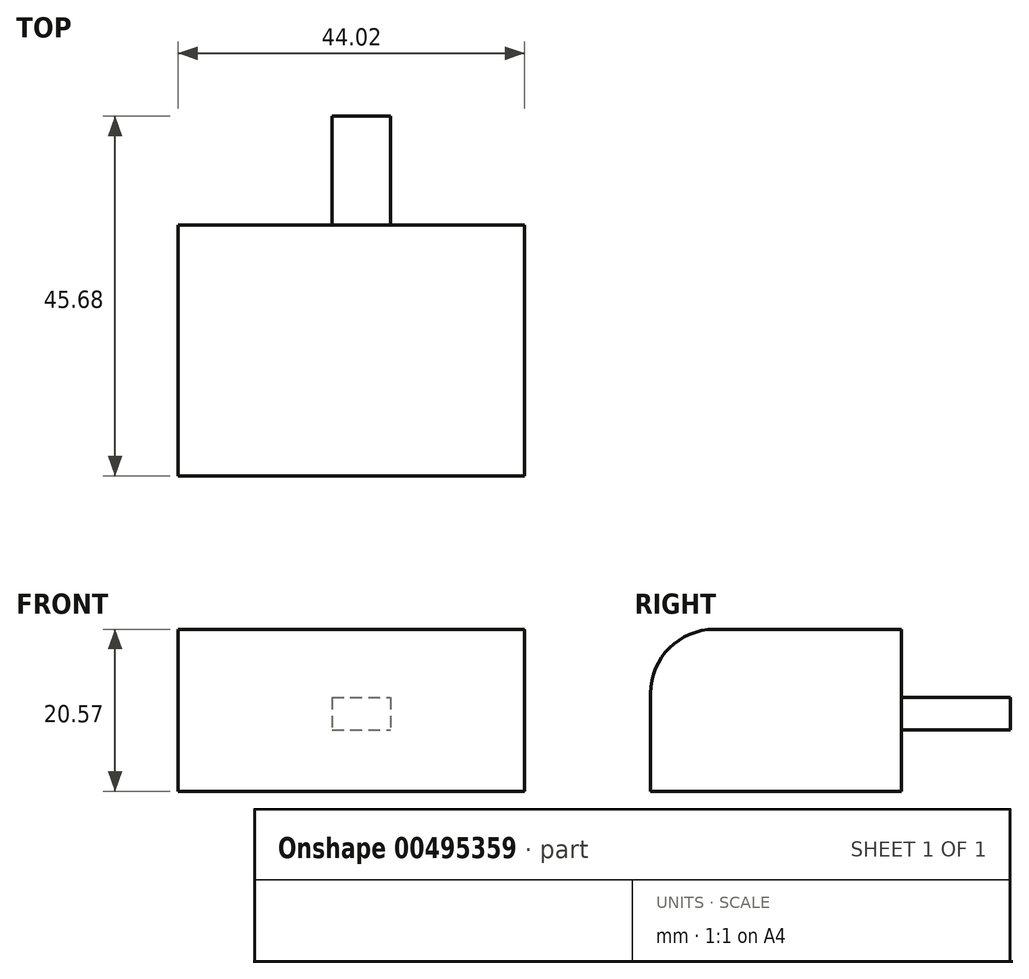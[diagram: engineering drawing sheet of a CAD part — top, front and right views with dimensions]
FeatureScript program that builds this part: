
annotation { "Feature Type Name" : "Feature", "Feature Type Description" : "" }
export const myFeature = defineFeature(function(context is Context, id is Id, definition is map)
    precondition{}
    {
        {
            var Q0;
            Q0=qCreatedBy(makeId("Front.planeOp"),FACE);
            var sketch = newSketch(context, id + "F0", { "sketchPlane" : qUnion([Q0])});
            skLineSegment(sketch, "E0.bottom", {"start": v(30.37, 0) * mm, "end": v(-13.65, 0) * mm});
            skLineSegment(sketch, "E0.top", {"start": v(30.37, 20.57) * mm, "end": v(-13.65, 20.57) * mm});
            skLineSegment(sketch, "E0.left", {"start": v(30.37, 0) * mm, "end": v(30.37, 20.57) * mm});
            skLineSegment(sketch, "E0.right", {"start": v(-13.65, 0) * mm, "end": v(-13.65, 20.57) * mm});
            skSolve(sketch);
        }
        {
            var Q0;
            Q0 = qSketchRegion(id + "F0", true);
            var Q1;
            Q1=makeQuery(id+"F0.imprint","IMPRINT",FACE,{"disambiguationData":[TD([[makeQuery(id+"F0.imprint","IMPRINT",EDGE,{"derivedFrom":sQuery(id+"F0.wireOp",EDGE,"E0.bottom")}),-1.0]])]});
            extrude(context, id + "F1", {"entities" : qUnion([Q0, Q1]), "depth" : 31.88 * mm});
        }
        {
            var Q0;
            Q0=makeQuery(id+"F1.opExtrude","CAP_EDGE",EDGE,{"disambiguationData":[OSD([sQuery(id+"F0.wireOp",EDGE,"E0.top")])],"isStart":false});
            fillet(context, id + "F2", {"entities" : qUnion([Q0]), "radius" : 8.14 * mm, "tangentPropagation" : true, "allowEdgeOverflow" : false});
        }
        {
            var Q0;
            Q0=makeQuery(id+"F1.opExtrude","CAP_FACE",FACE,{"disambiguationData":[OSD([sQuery(id+"F0.wireOp",EDGE,"E0.bottom"),sQuery(id+"F0.wireOp",EDGE,"E0.top"),sQuery(id+"F0.wireOp",EDGE,"E0.left"),sQuery(id+"F0.wireOp",EDGE,"E0.right")])],"isStart":true});
            var sketch = newSketch(context, id + "F3", { "sketchPlane" : qUnion([Q0])});
            skLineSegment(sketch, "E1.bottom", {"start": v(-5.93, 11.9) * mm, "end": v(-13.3, 11.9) * mm});
            skLineSegment(sketch, "E1.top", {"start": v(-5.93, 7.77) * mm, "end": v(-13.3, 7.77) * mm});
            skLineSegment(sketch, "E1.left", {"start": v(-5.93, 11.9) * mm, "end": v(-5.93, 7.77) * mm});
            skLineSegment(sketch, "E1.right", {"start": v(-13.3, 11.9) * mm, "end": v(-13.3, 7.77) * mm});
            skSolve(sketch);
        }
        {
            var Q0;
            Q0 = qSketchRegion(id + "F3", true);
            extrude(context, id + "F4", {"entities" : qUnion([Q0]), "operationType" : NewBodyOperationType.ADD, "depth" : 13.8 * mm});
        }
    });
